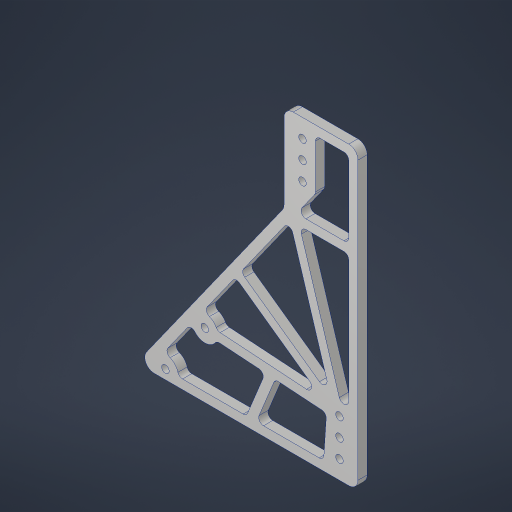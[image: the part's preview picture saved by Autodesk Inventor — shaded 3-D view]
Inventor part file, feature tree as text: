
AUTODESK INVENTOR PART (.ipt)
format: ipt  version: 2023.4 (Build 274418000, 418)  size: 400,896 bytes
history: native  units: in
note: dims shown in document units (in); Inventor stores cm internally (conversion verified against a paired STEP export)
features: sketch x5, projected_geometry x5, extrude x3, hole x2, fillet x2
ambient origin geometry x8: Origin, YZ Plane, XZ Plane, XY Plane, X Axis, Y Axis, Z Axis, Center Point
bodies: Solid1 (feature_tree)
feature tree (17):
  extrude  "Extrusion1"  Depth=1.0in
  hole  "Hole1"  [1 undecoded]
  sketch  "Sketch3"  dims[d5=0.5in d6=0.5in]
  extrude  "Extrusion2"  Depth=0.5in
  hole  "Hole2"  [1 undecoded]
  extrude  "Extrusion3"  Depth=0.25in
  fillet  "Fillet1"  Radius=0.125in
  fillet  "Fillet2"  Radius=0.125in
  sketch  "Sketch2"  dims[d3=0.0in d4=1.0in]
  sketch  "Sketch4"  dims[d7=0.5in d8=0.5in]
  sketch  "Sketch5"  dims[d9=0.5in d10=0.5in]
  projected_geometry  "Projected Loop1"
  sketch  "Sketch6"  dims[d11=1.0in d12=0.201in d13=0.75in d14=0.385in d15=0.25in d16=0.5635in d17=1.0in d18=0.8108in d19=0.25in d20=0.125in d21=0.125in d22=0.25in d23=0.25in d24=0.25in d25=0.25in d26=0.25in d27=0.25in d28=0.125in d29=0.125in d30=0.125in d31=0.125in d32=2.0in d33=6.0in d34=1.0in d35=0.0in d36=0.375in d37=0.375in d38=0.5in d39=1.0in d40=0.201in d41=0.75in d42=0.375in d43=0.25in d44=0.5635in d45=1.0in d46=0.8108in d47=2.375in d48=10.0in d49=2.0in d50=0.0625in d51=0.378in d52=0.5in d54=0.25in d55=0.25in d56=0.25in d57=0.25in d58=0.25in d59=0.25in d60=0.25in d61=0.25in d62=0.125in d63=0.125in d64=0.125in d65=0.125in d66=0.25in d67=0.25in d68=0.125in d69=0.25in d70=0.125in d71=0.25in d72=0.125in d73=0.25in d74=0.0in d75=0.0in d76=0.25in d77=0.13in]
  projected_geometry  "Project Cut Edges1"
  projected_geometry  "Project Cut Edges2"
  projected_geometry  "Project Cut Edges3"
  projected_geometry  "Project Cut Edges4"
note: 2 required parameter values undecoded (feature->parameter linkage not recoverable at this tier; creation-order binding heuristic only, values carry confidence <= 0.55)
